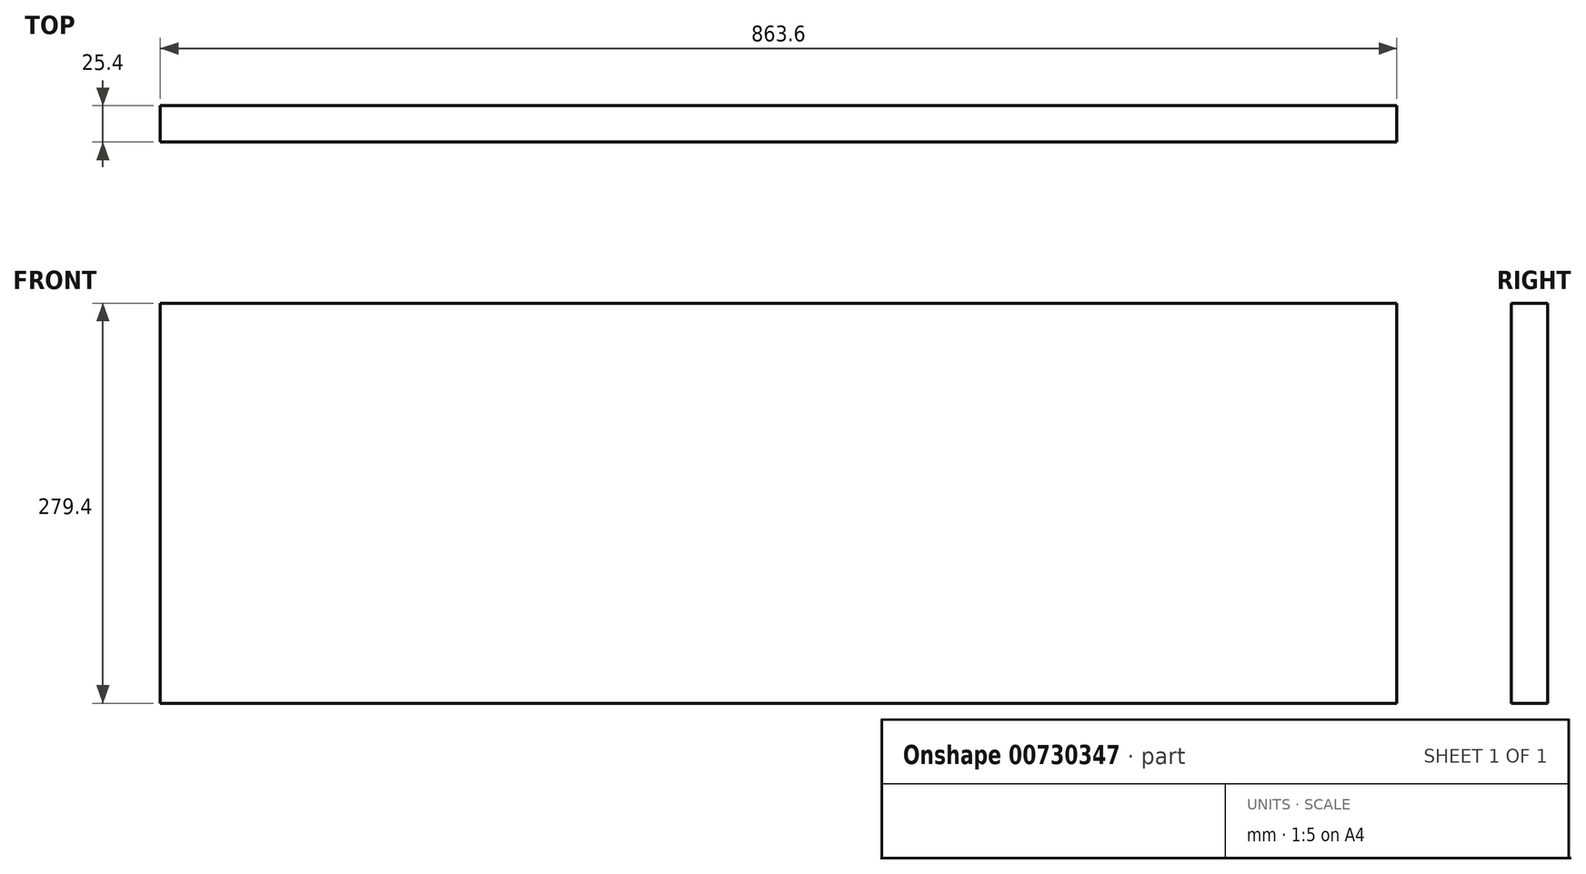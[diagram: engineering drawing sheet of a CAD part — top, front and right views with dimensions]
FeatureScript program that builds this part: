
annotation { "Feature Type Name" : "Feature", "Feature Type Description" : "" }
export const myFeature = defineFeature(function(context is Context, id is Id, definition is map)
    precondition{}
    {
        {
            var Q0;
            Q0=qCreatedBy(makeId("Top.planeOp"),FACE);
            var sketch = newSketch(context, id + "F0", { "sketchPlane" : qUnion([Q0])});
            skLineSegment(sketch, "E0.bottom", {"start": v(431.8, -12.7) * mm, "end": v(-431.8, -12.7) * mm});
            skLineSegment(sketch, "E0.top", {"start": v(431.8, 12.7) * mm, "end": v(-431.8, 12.7) * mm});
            skLineSegment(sketch, "E0.left", {"start": v(431.8, -12.7) * mm, "end": v(431.8, 12.7) * mm});
            skLineSegment(sketch, "E0.right", {"start": v(-431.8, -12.7) * mm, "end": v(-431.8, 12.7) * mm});
            skPoint(sketch, "E0.middle", {"position": v(0, 0) * mm});
            skSolve(sketch);
        }
        {
            var Q0;
            Q0 = qSketchRegion(id + "F0", true);
            extrude(context, id + "F1", {"entities" : qUnion([Q0]), "endBound" : BoundingType.SYMMETRIC, "depth" : 279.4 * mm, "offsetDistance" : 25.4 * mm});
        }
    });
